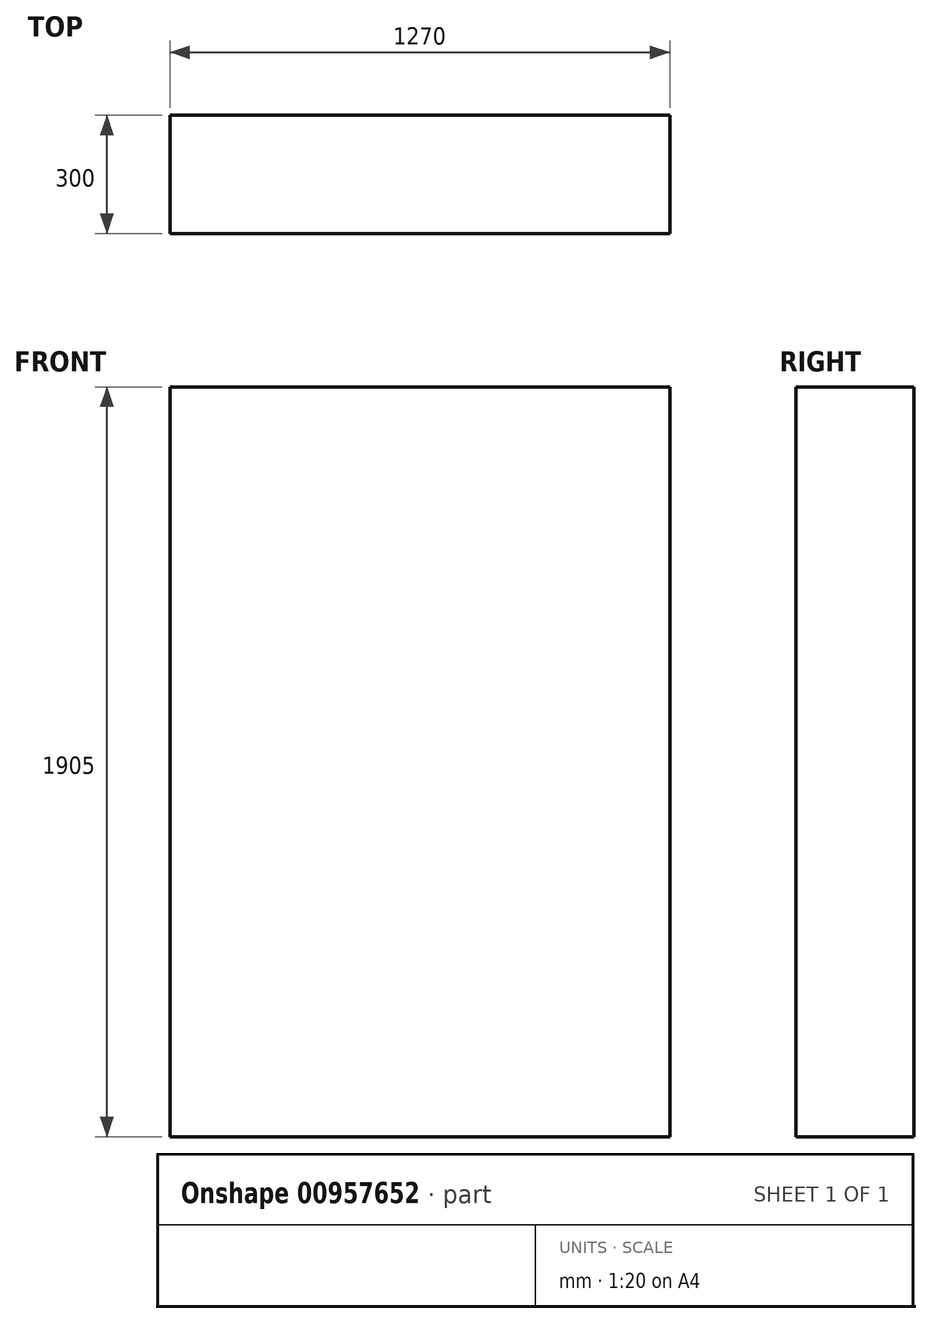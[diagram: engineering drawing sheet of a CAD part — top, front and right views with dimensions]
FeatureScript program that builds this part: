
annotation { "Feature Type Name" : "Feature", "Feature Type Description" : "" }
export const myFeature = defineFeature(function(context is Context, id is Id, definition is map)
    precondition{}
    {
        {
            var Q0;
            Q0=qCreatedBy(makeId("Front.planeOp"),FACE);
            var sketch = newSketch(context, id + "F0", { "sketchPlane" : qUnion([Q0])});
            skLineSegment(sketch, "E0.bottom", {"start": v(0, 0) * mm, "end": v(1270, 0) * mm});
            skLineSegment(sketch, "E0.top", {"start": v(0, 1905) * mm, "end": v(1270, 1905) * mm});
            skLineSegment(sketch, "E0.left", {"start": v(0, 0) * mm, "end": v(0, 1905) * mm});
            skLineSegment(sketch, "E0.right", {"start": v(1270, 0) * mm, "end": v(1270, 1905) * mm});
            skSolve(sketch);
        }
        {
            var Q0;
            Q0=makeQuery(id+"F0.imprint","IMPRINT",FACE,{"disambiguationData":[TD([[makeQuery(id+"F0.imprint","IMPRINT",EDGE,{"derivedFrom":sQuery(id+"F0.wireOp",EDGE,"E0.bottom")}),1.0]])]});
            extrude(context, id + "F1", {"entities" : qUnion([Q0]), "depth" : 300 * mm, "offsetDistance" : 25.4 * mm});
        }
    });
